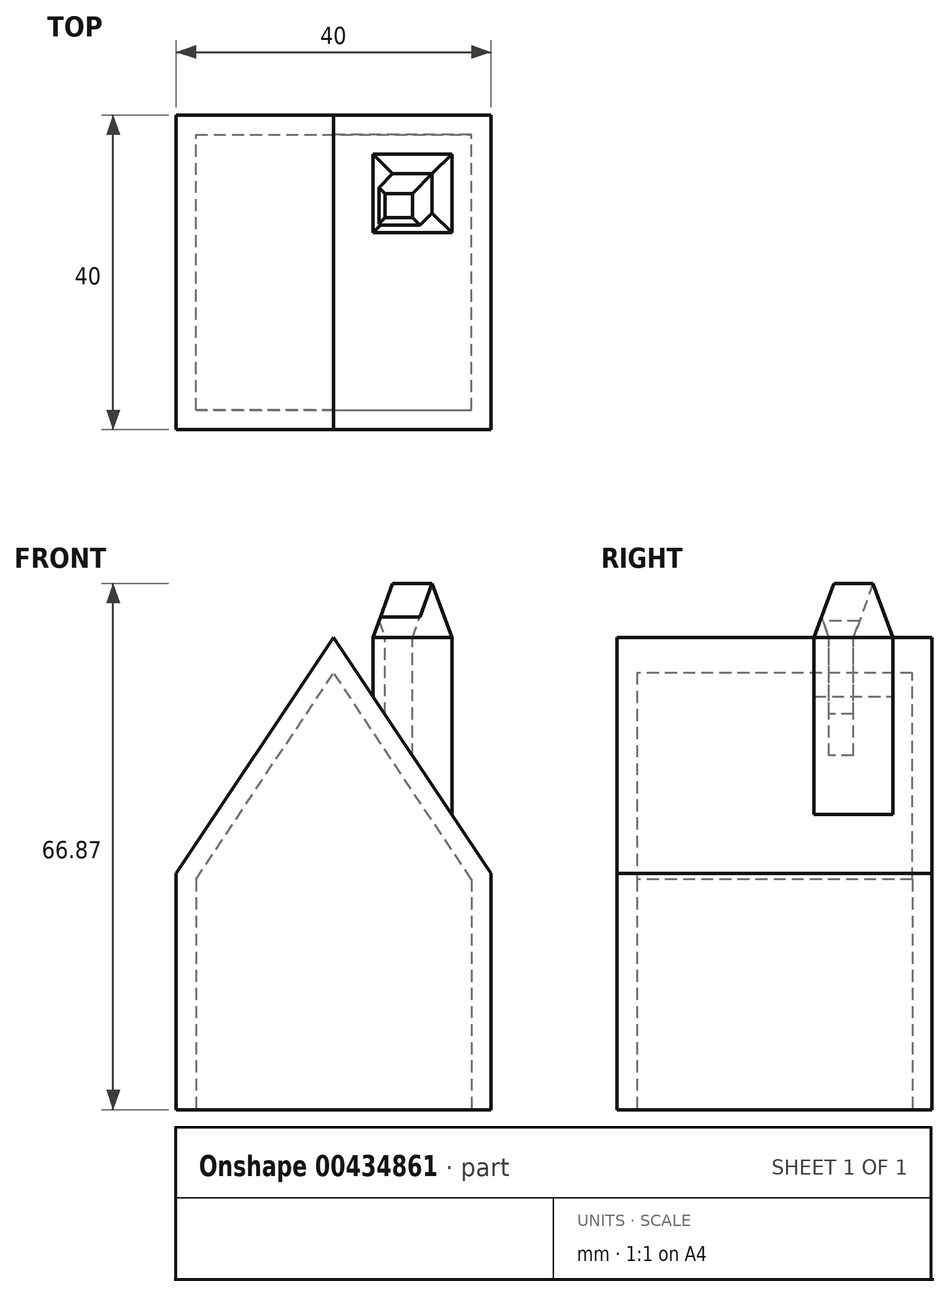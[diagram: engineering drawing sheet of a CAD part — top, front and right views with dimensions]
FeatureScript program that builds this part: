
annotation { "Feature Type Name" : "Feature", "Feature Type Description" : "" }
export const myFeature = defineFeature(function(context is Context, id is Id, definition is map)
    precondition{}
    {
        {
            var Q0;
            Q0=qCreatedBy(makeId("Top.planeOp"),FACE);
            var sketch = newSketch(context, id + "F0", { "sketchPlane" : qUnion([Q0])});
            skLineSegment(sketch, "E0.bottom", {"start": v(0, 0) * mm, "end": v(40, 0) * mm});
            skLineSegment(sketch, "E0.top", {"start": v(0, 40) * mm, "end": v(40, 40) * mm});
            skLineSegment(sketch, "E0.left", {"start": v(0, 0) * mm, "end": v(0, 40) * mm});
            skLineSegment(sketch, "E0.right", {"start": v(40, 0) * mm, "end": v(40, 40) * mm});
            skSolve(sketch);
        }
        {
            var Q0;
            Q0 = qSketchRegion(id + "F0", true);
            extrude(context, id + "F1", {"entities" : qUnion([Q0]), "depth" : 60 * mm});
        }
        {
            var Q0;
            Q0=makeQuery(id+"F1.opExtrude","SWEPT_FACE",FACE,{"disambiguationData":[OSD([sQuery(id+"F0.wireOp",EDGE,"E0.bottom")])]});
            var sketch = newSketch(context, id + "F2", { "sketchPlane" : qUnion([Q0])});
            skLineSegment(sketch, "E1", {"start": v(20, 60) * mm, "end": v(0, 30) * mm});
            skLineSegment(sketch, "E2", {"start": v(0, 30) * mm, "end": v(0, 60) * mm});
            skLineSegment(sketch, "E3", {"start": v(0, 60) * mm, "end": v(20, 60) * mm});
            skLineSegment(sketch, "E4", {"start": v(20, 60) * mm, "end": v(40, 30) * mm});
            skLineSegment(sketch, "E5", {"start": v(40, 30) * mm, "end": v(40, 60) * mm});
            skLineSegment(sketch, "E6", {"start": v(40, 60) * mm, "end": v(20, 60) * mm});
            skSolve(sketch);
        }
        {
            var Q0;
            Q0 = qSketchRegion(id + "F2", true);
            extrude(context, id + "F3", {"entities" : qUnion([Q0]), "operationType" : NewBodyOperationType.REMOVE, "endBound" : BoundingType.THROUGH_ALL, "oppositeDirection" : true, "depth" : 40 * mm});
        }
        {
            var Q0;
            Q0=makeQuery(id+"F1.opExtrude","CAP_FACE",FACE,{"disambiguationData":[OSD([sQuery(id+"F0.wireOp",EDGE,"E0.bottom"),sQuery(id+"F0.wireOp",EDGE,"E0.top"),sQuery(id+"F0.wireOp",EDGE,"E0.left"),sQuery(id+"F0.wireOp",EDGE,"E0.right")])],"isStart":true});
            shell(context, id + "F4", {"entities" : qUnion([Q0]), "thickness" : 2.5 * mm});
        }
        {
            var Q0;
            Q0=makeQuery(id+"F3.boolean.opBoolean","INTERSECT",VERTEX,{"derivedFrom":[makeQuery(id+"F1.opExtrude","SWEPT_FACE",FACE,{"disambiguationData":[OSD([sQuery(id+"F0.wireOp",EDGE,"E0.top")])]}),makeQuery(id+"F3.opExtrude","SWEPT_FACE",FACE,{"disambiguationData":[OSD([sQuery(id+"F2.wireOp",EDGE,"E1")])]}),makeQuery(id+"F3.opExtrude","SWEPT_FACE",FACE,{"disambiguationData":[OSD([sQuery(id+"F2.wireOp",EDGE,"E4")])]})]});
            var Q1;
            Q1=makeQuery(id+"F1.opExtrude","SWEPT_EDGE",EDGE,{"disambiguationData":[OSD([sQuery(id+"F0.wireOp",EDGE,"E0.bottom"),sQuery(id+"F0.wireOp",EDGE,"E0.right")])]});
            cPlane(context, id + "F5", {"entities" : qUnion([Q0, Q1]), "cplaneType" : CPlaneType.LINE_POINT, "offset" : 25 * mm, "width" : 150 * mm, "height" : 150 * mm});
        }
        {
            var Q0;
            Q0=qCreatedBy(id+"F5.planeOp",FACE);
            var sketch = newSketch(context, id + "F6", { "sketchPlane" : qUnion([Q0])});
            skLineSegment(sketch, "E7.bottom", {"start": v(25, -25.03) * mm, "end": v(35, -25.03) * mm});
            skLineSegment(sketch, "E7.top", {"start": v(25, -35.03) * mm, "end": v(35, -35.03) * mm});
            skLineSegment(sketch, "E7.left", {"start": v(25, -25.03) * mm, "end": v(25, -35.03) * mm});
            skLineSegment(sketch, "E7.right", {"start": v(35, -25.03) * mm, "end": v(35, -35.03) * mm});
            skLineSegment(sketch, "E8.bottom", {"start": v(25, -35.03) * mm, "end": v(20, -35.03) * mm, "construction": true});
            skLineSegment(sketch, "E8.top", {"start": v(25, -40) * mm, "end": v(20, -40) * mm, "construction": true});
            skLineSegment(sketch, "E8.left", {"start": v(25, -35.03) * mm, "end": v(25, -40) * mm, "construction": true});
            skLineSegment(sketch, "E8.right", {"start": v(20, -35.03) * mm, "end": v(20, -40) * mm, "construction": true});
            skPoint(sketch, "E9.firstSnap0", {"position": v(25, -30.03) * mm});
            skPoint(sketch, "E9.firstSnap1", {"position": v(30, -25.03) * mm});
            skLineSegment(sketch, "E9.bottom", {"start": v(30, -30.03) * mm, "end": v(26.5, -30.03) * mm});
            skLineSegment(sketch, "E9.top", {"start": v(30, -26.92) * mm, "end": v(26.5, -26.92) * mm});
            skLineSegment(sketch, "E9.left", {"start": v(30, -30.03) * mm, "end": v(30, -26.92) * mm});
            skLineSegment(sketch, "E9.right", {"start": v(26.5, -30.03) * mm, "end": v(26.5, -26.92) * mm});
            skSolve(sketch);
        }
        {
            var Q0;
            Q0 = qSketchRegion(id + "F6", true);
            extrude(context, id + "F7", {"entities" : qUnion([Q0]), "operationType" : NewBodyOperationType.ADD, "endBound" : BoundingType.UP_TO_NEXT, "depth" : 25 * mm, "hasSecondDirection" : true, "secondDirectionOppositeDirection" : true, "secondDirectionDepth" : 10 * mm, "hasSecondDirectionDraft" : true, "secondDirectionDraftAngle" : 20 * degree, "secondDirectionDraftPullDirection" : true});
        }
    });
